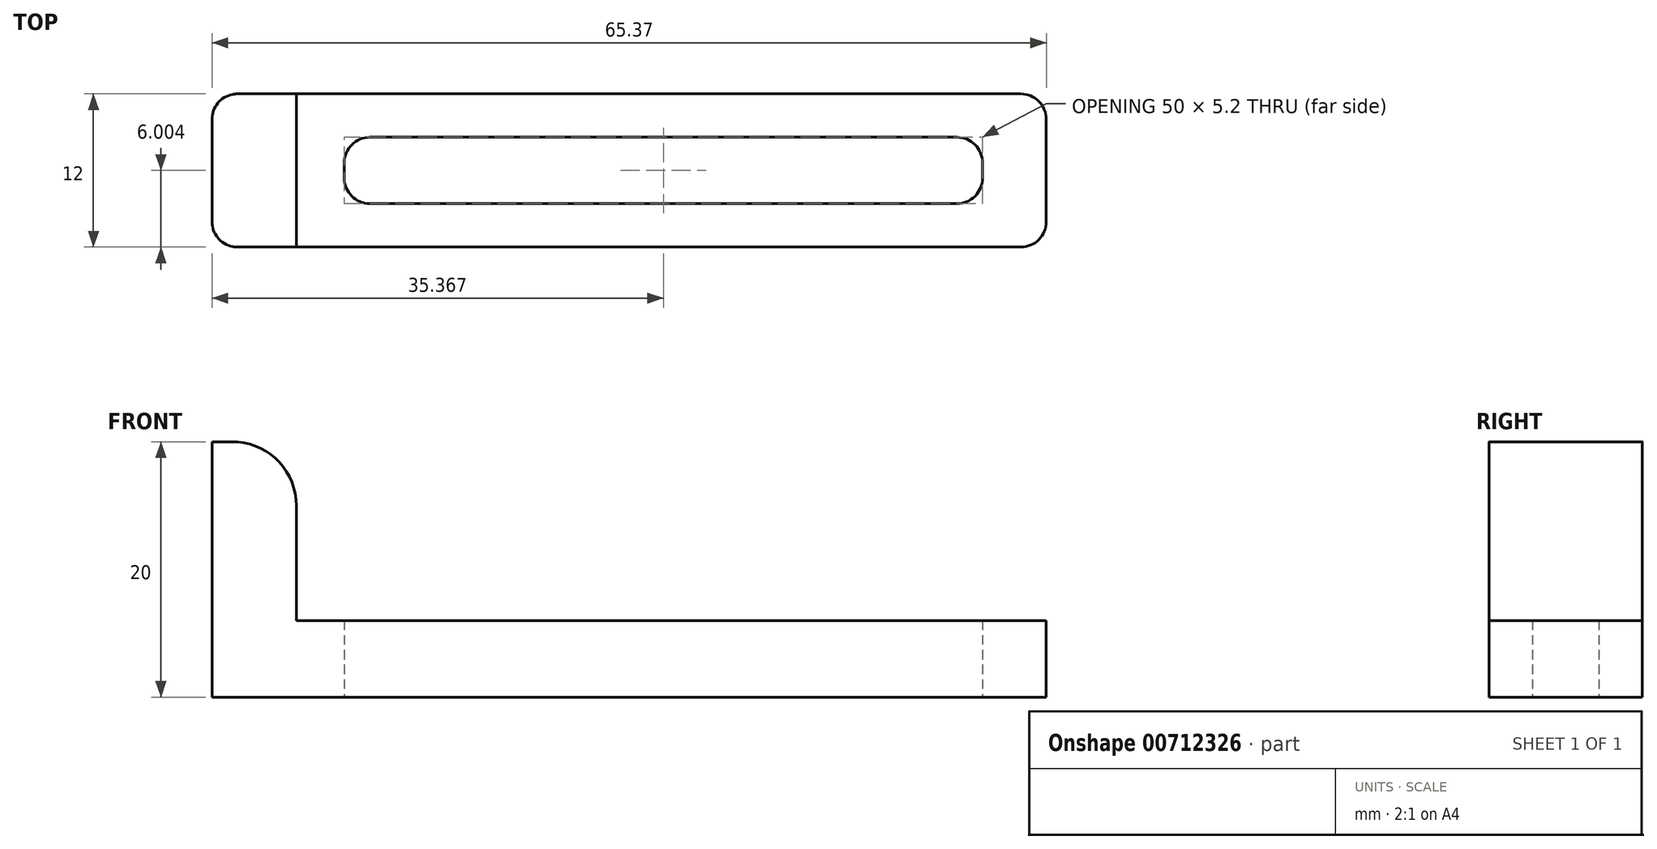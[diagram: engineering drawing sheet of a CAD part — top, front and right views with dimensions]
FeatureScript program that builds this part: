
annotation { "Feature Type Name" : "Feature", "Feature Type Description" : "" }
export const myFeature = defineFeature(function(context is Context, id is Id, definition is map)
    precondition{}
    {
        {
            var Q0;
            Q0=qCreatedBy(makeId("Top.planeOp"),FACE);
            var sketch = newSketch(context, id + "F0", { "sketchPlane" : qUnion([Q0])});
            skLineSegment(sketch, "E0", {"start": v(-31.9, 32.72) * mm, "end": v(42.95, 32.72) * mm, "construction": true});
            skPoint(sketch, "E0.startSnap0", {"position": v(-27.32, 32.72) * mm});
            skLineSegment(sketch, "E1.0", {"start": v(-22.42, 38.72) * mm, "end": v(42.95, 38.72) * mm});
            skLineSegment(sketch, "E2.0", {"start": v(-22.42, 26.72) * mm, "end": v(42.95, 26.72) * mm});
            skPoint(sketch, "E3.newPointB", {"position": v(38.74, 27.72) * mm});
            skPoint(sketch, "E4.newPointA", {"position": v(38.74, 37.72) * mm});
            skLineSegment(sketch, "E5", {"start": v(42.95, 38.72) * mm, "end": v(42.95, 26.72) * mm});
            skLineSegment(sketch, "E6.0", {"start": v(37.95, 35.32) * mm, "end": v(37.95, 30.12) * mm});
            skLineSegment(sketch, "E7", {"start": v(-22.42, 38.72) * mm, "end": v(-22.42, 26.72) * mm});
            skLineSegment(sketch, "E8", {"start": v(-15.81, 38.72) * mm, "end": v(-15.81, 26.72) * mm});
            skPoint(sketch, "E9.orphan", {"position": v(-27.32, 27.72) * mm});
            skPoint(sketch, "E10.left.end.orphan", {"position": v(-27.32, 37.72) * mm});
            skLineSegment(sketch, "E11", {"start": v(37.95, 35.32) * mm, "end": v(-12.05, 35.32) * mm});
            skLineSegment(sketch, "E12", {"start": v(37.95, 30.12) * mm, "end": v(-12.05, 30.12) * mm});
            skLineSegment(sketch, "E13", {"start": v(-12.05, 35.32) * mm, "end": v(-12.05, 30.12) * mm});
            skSolve(sketch);
        }
        {
            var Q0;
            {var subQ0=sQuery(id+"F0.wireOp",EDGE,"E5");Q0=makeQuery(id+"F0.imprint","IMPRINT",FACE,{"disambiguationData":[TD([[makeQuery(id+"F0.imprint","IMPRINT",EDGE,{"derivedFrom":subQ0}),-1.0]])]});}
            extrude(context, id + "F1", {"entities" : qUnion([Q0]), "depth" : 6 * mm, "offsetDistance" : 25 * mm});
        }
        {
            var Q0;
            {var subQ2=sQuery(id+"F0.wireOp",EDGE,"E7");Q0=makeQuery(id+"F0.imprint","IMPRINT",FACE,{"disambiguationData":[TD([[makeQuery(id+"F0.imprint","IMPRINT",EDGE,{"derivedFrom":subQ2}),1.0]])]});}
            extrude(context, id + "F2", {"entities" : qUnion([Q0]), "operationType" : NewBodyOperationType.ADD, "depth" : 20 * mm, "offsetDistance" : 25 * mm});
        }
        {
            var Q0;
            Q0=makeQuery(id+"F1.opExtrude","SWEPT_EDGE",EDGE,{"disambiguationData":[OSD([sQuery(id+"F0.wireOp",EDGE,"E2.0"),sQuery(id+"F0.wireOp",EDGE,"E5")])]});
            fillet(context, id + "F3", {"entities" : qUnion([Q0]), "tangentPropagation" : true, "radius" : 2 * mm, "defaultsChanged" : true, "vertexSettings" : [], "allowEdgeOverflow" : false});
        }
        {
            var Q0;
            Q0=makeQuery(id+"F1.opExtrude","SWEPT_EDGE",EDGE,{"disambiguationData":[OSD([sQuery(id+"F0.wireOp",EDGE,"E1.0"),sQuery(id+"F0.wireOp",EDGE,"E5")])]});
            fillet(context, id + "F4", {"entities" : qUnion([Q0]), "tangentPropagation" : true, "radius" : 2 * mm, "defaultsChanged" : true, "vertexSettings" : [], "allowEdgeOverflow" : false});
        }
        {
            var Q0;
            Q0=makeQuery(id+"F1.opExtrude","SWEPT_EDGE",EDGE,{"disambiguationData":[OSD([sQuery(id+"F0.wireOp",EDGE,"E11"),sQuery(id+"F0.wireOp",EDGE,"E13")])]});
            var Q1;
            Q1=makeQuery(id+"F1.opExtrude","SWEPT_EDGE",EDGE,{"disambiguationData":[OSD([sQuery(id+"F0.wireOp",EDGE,"E6.0"),sQuery(id+"F0.wireOp",EDGE,"E11")])]});
            var Q2;
            Q2=makeQuery(id+"F1.opExtrude","SWEPT_EDGE",EDGE,{"disambiguationData":[OSD([sQuery(id+"F0.wireOp",EDGE,"E6.0"),sQuery(id+"F0.wireOp",EDGE,"E12")])]});
            var Q3;
            Q3=makeQuery(id+"F1.opExtrude","SWEPT_EDGE",EDGE,{"disambiguationData":[OSD([sQuery(id+"F0.wireOp",EDGE,"E12"),sQuery(id+"F0.wireOp",EDGE,"E13")])]});
            fillet(context, id + "F5", {"entities" : qUnion([Q0, Q1, Q2, Q3]), "tangentPropagation" : true, "radius" : 2 * mm, "defaultsChanged" : true, "vertexSettings" : [], "allowEdgeOverflow" : false});
        }
        {
            var Q0;
            Q0=makeQuery(id+"F2.opExtrude","SWEPT_EDGE",EDGE,{"disambiguationData":[OSD([sQuery(id+"F0.wireOp",EDGE,"E1.0"),sQuery(id+"F0.wireOp",EDGE,"E7")])]});
            var Q1;
            Q1=makeQuery(id+"F2.opExtrude","SWEPT_EDGE",EDGE,{"disambiguationData":[OSD([sQuery(id+"F0.wireOp",EDGE,"E2.0"),sQuery(id+"F0.wireOp",EDGE,"E7")])]});
            fillet(context, id + "F6", {"entities" : qUnion([Q0, Q1]), "tangentPropagation" : true, "radius" : 2 * mm, "defaultsChanged" : true, "vertexSettings" : [], "allowEdgeOverflow" : false});
        }
        {
            var Q0;
            Q0=makeQuery(id+"F2.opExtrude","CAP_EDGE",EDGE,{"disambiguationData":[OSD([sQuery(id+"F0.wireOp",EDGE,"E8")])],"isStart":false});
            fillet(context, id + "F7", {"entities" : qUnion([Q0]), "tangentPropagation" : true, "radius" : 5 * mm, "defaultsChanged" : false, "vertexSettings" : [], "allowEdgeOverflow" : false});
        }
    });
